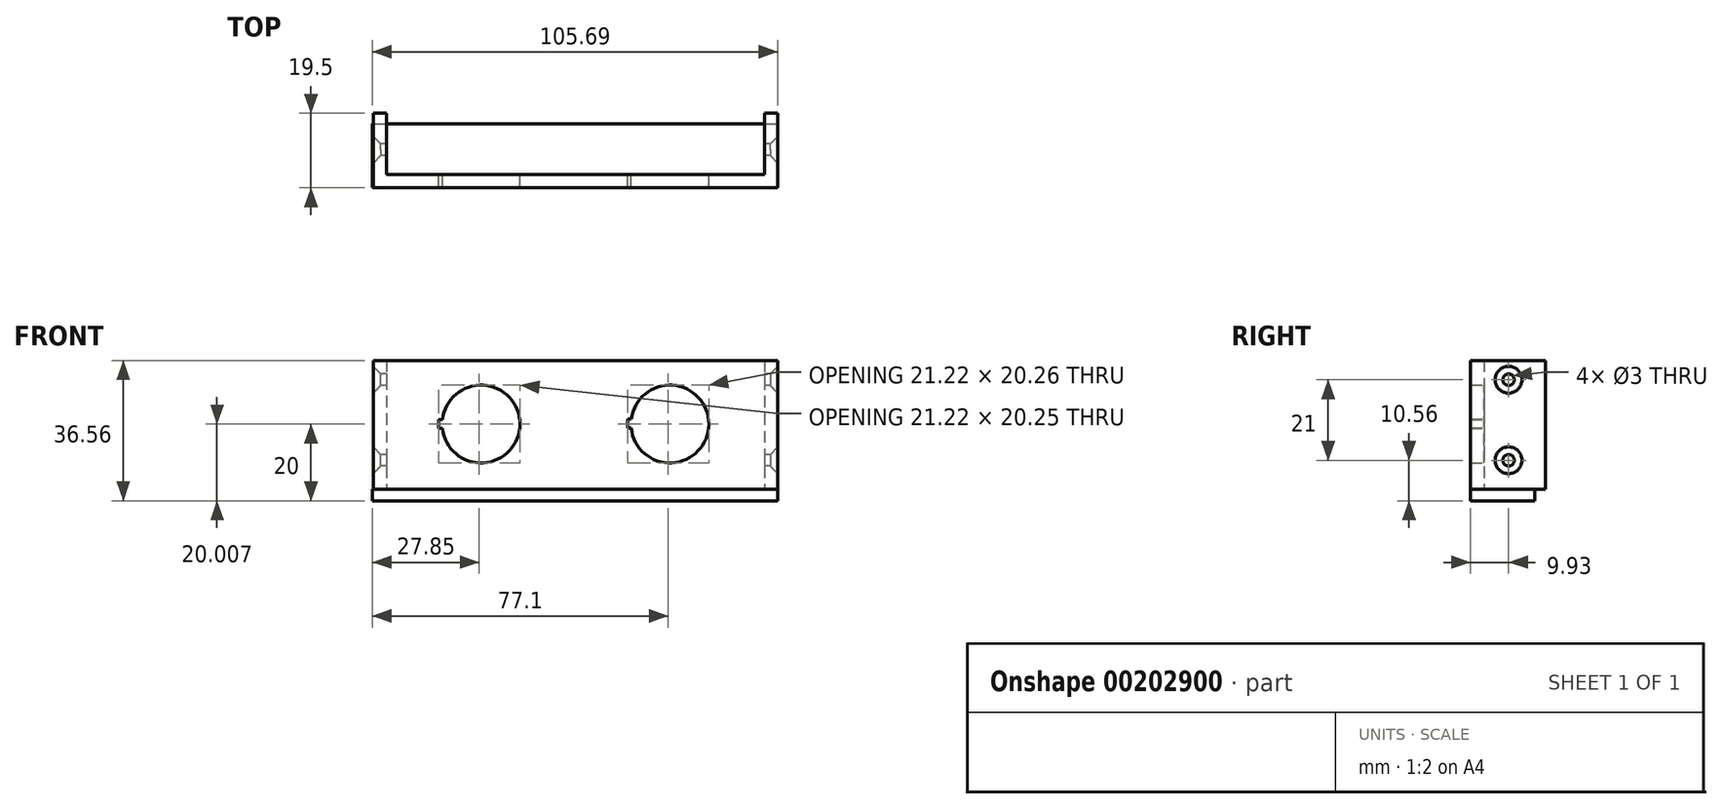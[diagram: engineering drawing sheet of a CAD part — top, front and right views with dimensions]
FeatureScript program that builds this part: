
annotation { "Feature Type Name" : "Feature", "Feature Type Description" : "" }
export const myFeature = defineFeature(function(context is Context, id is Id, definition is map)
    precondition{}
    {
        {
            var Q0;
            Q0=qCreatedBy(makeId("Front.planeOp"),FACE);
            var sketch = newSketch(context, id + "F0", { "sketchPlane" : qUnion([Q0])});
            skLineSegment(sketch, "E0.bottom", {"start": v(-49.25, 16.56) * mm, "end": v(49.25, 16.56) * mm});
            skLineSegment(sketch, "E0.top", {"start": v(-49.25, -17) * mm, "end": v(49.25, -17) * mm});
            skLineSegment(sketch, "E1", {"start": v(0, 48.82) * mm, "end": v(0, -71.11) * mm, "construction": true});
            skLineSegment(sketch, "E2", {"start": v(-61.05, 0) * mm, "end": v(79.23, 0) * mm, "construction": true});
            skLineSegment(sketch, "E3", {"start": v(-49.25, 16.56) * mm, "end": v(-49.25, -17) * mm});
            skLineSegment(sketch, "E4", {"start": v(49.25, 16.56) * mm, "end": v(49.25, -17) * mm});
            skLineSegment(sketch, "E5", {"start": v(-24.63, 20.87) * mm, "end": v(-24.62, -26.06) * mm, "construction": true});
            skLineSegment(sketch, "E6.MirrorCS", {"start": v(24.62, 20.87) * mm, "end": v(24.63, -26.06) * mm, "construction": true});
            skArc(sketch, "E7", {"start": v(-34.7, -1.15) * mm, "mid": v(-14.48, 0) * mm, "end": v(-34.7, 1.15) * mm});
            skLineSegment(sketch, "E8.bottom", {"start": v(-35.7, 1.15) * mm, "end": v(-34.7, 1.15) * mm});
            skLineSegment(sketch, "E8.top", {"start": v(-35.7, -1.15) * mm, "end": v(-34.7, -1.15) * mm});
            skLineSegment(sketch, "E8.left", {"start": v(-35.7, 1.15) * mm, "end": v(-35.7, -1.15) * mm});
            skArc(sketch, "E9", {"start": v(14.53, -1.05) * mm, "mid": v(34.77, -0.1) * mm, "end": v(14.55, 1.25) * mm});
            skLineSegment(sketch, "E10.bottom", {"start": v(13.55, 1.25) * mm, "end": v(14.55, 1.25) * mm});
            skLineSegment(sketch, "E10.top", {"start": v(13.55, -1.05) * mm, "end": v(14.53, -1.05) * mm});
            skLineSegment(sketch, "E10.left", {"start": v(13.55, 1.25) * mm, "end": v(13.55, -1.05) * mm});
            skLineSegment(sketch, "E11.MirrorCS", {"start": v(49.25, -17) * mm, "end": v(-24.62, -17) * mm});
            skPoint(sketch, "E12.orphan", {"position": v(-52.75, 16.56) * mm});
            skPoint(sketch, "E13.orphan", {"position": v(-52.75, -17) * mm});
            skPoint(sketch, "E14.orphan", {"position": v(52.75, 16.56) * mm});
            skPoint(sketch, "E15.MirrorCS.end.orphan", {"position": v(49.25, 16.56) * mm});
            skPoint(sketch, "E16.MirrorCS.end.orphan", {"position": v(52.75, -17) * mm});
            skLineSegment(sketch, "E17.bottom", {"start": v(-52.75, 16.56) * mm, "end": v(-49.25, 16.56) * mm});
            skLineSegment(sketch, "E17.top", {"start": v(-52.75, -17) * mm, "end": v(-49.25, -17) * mm});
            skLineSegment(sketch, "E17.left", {"start": v(-52.75, 16.56) * mm, "end": v(-52.75, -17) * mm});
            skLineSegment(sketch, "E18.bottom", {"start": v(49.25, 16.56) * mm, "end": v(52.75, 16.56) * mm});
            skLineSegment(sketch, "E18.top", {"start": v(49.25, -17) * mm, "end": v(52.75, -17) * mm});
            skLineSegment(sketch, "E18.right", {"start": v(52.75, 16.56) * mm, "end": v(52.75, -17) * mm});
            skSolve(sketch);
        }
        {
            var Q0;
            Q0 = qSketchRegion(id + "F0", true);
            extrude(context, id + "F1", {"entities" : qUnion([Q0]), "depth" : 3.5 * mm});
        }
        {
            var Q0;
            Q0=makeQuery(id+"F0.imprint","IMPRINT",FACE,{"disambiguationData":[TD([[makeQuery(id+"F0.imprint","IMPRINT",EDGE,{"derivedFrom":sQuery(id+"F0.wireOp",EDGE,"E3")}),-1.0]])]});
            var Q1;
            Q1=makeQuery(id+"F0.imprint","IMPRINT",FACE,{"disambiguationData":[TD([[makeQuery(id+"F0.imprint","IMPRINT",EDGE,{"derivedFrom":sQuery(id+"F0.wireOp",EDGE,"E18.bottom")}),-1.0]])]});
            extrude(context, id + "F2", {"entities" : qUnion([Q0, Q1]), "operationType" : NewBodyOperationType.ADD, "oppositeDirection" : true, "depth" : 16 * mm});
        }
        {
            var Q0;
            {var subQ0=sQuery(id+"F0.wireOp",EDGE,"E18.top");var subQ1=sQuery(id+"F0.wireOp",EDGE,"E17.top");Q0=makeQuery(id+"F2.boolean.opBoolean","MERGE",FACE,{"derivedFrom":[makeQuery(id+"F1.opExtrude","SWEPT_FACE",FACE,{"disambiguationData":[OSD([sQuery(id+"F0.wireOp",EDGE,"E0.top"),sQuery(id+"F0.wireOp",EDGE,"E11.MirrorCS"),subQ1,subQ0])]}),makeQuery(id+"F2.opExtrude","SWEPT_FACE",FACE,{"disambiguationData":[OSD([subQ1])]}),makeQuery(id+"F2.opExtrude","SWEPT_FACE",FACE,{"disambiguationData":[OSD([subQ0])]})]});}
            cPlane(context, id + "F3", {"entities" : qUnion([Q0]), "cplaneType" : CPlaneType.OFFSET, "offset" : 0 * mm, "width" : 150 * mm, "height" : 150 * mm});
        }
        {
            var Q0;
            Q0=qCreatedBy(id+"F3.planeOp",FACE);
            var sketch = newSketch(context, id + "F4", { "sketchPlane" : qUnion([Q0])});
            skLineSegment(sketch, "E19.bottom", {"start": v(-52.94, 3.5) * mm, "end": v(52.75, 3.5) * mm});
            skLineSegment(sketch, "E19.top", {"start": v(-52.94, -13.25) * mm, "end": v(52.75, -13.25) * mm});
            skLineSegment(sketch, "E19.left", {"start": v(-52.94, 3.5) * mm, "end": v(-52.94, -13.25) * mm});
            skLineSegment(sketch, "E19.right", {"start": v(52.75, 3.5) * mm, "end": v(52.75, -13.25) * mm});
            skSolve(sketch);
        }
        {
            var Q0;
            Q0 = qSketchRegion(id + "F4", true);
            extrude(context, id + "F5", {"entities" : qUnion([Q0]), "depth" : 3 * mm});
        }
        {
            var Q0;
            {var subQ0=sQuery(id+"F0.wireOp",EDGE,"E17.left");Q0=makeQuery(id+"F2.boolean.opBoolean","MERGE",FACE,{"derivedFrom":[makeQuery(id+"F1.opExtrude","SWEPT_FACE",FACE,{"disambiguationData":[OSD([subQ0])]}),makeQuery(id+"F2.opExtrude","SWEPT_FACE",FACE,{"disambiguationData":[OSD([subQ0])]})]});}
            cPlane(context, id + "F6", {"entities" : qUnion([Q0]), "cplaneType" : CPlaneType.OFFSET, "offset" : 25 * mm, "width" : 150 * mm, "height" : 150 * mm});
        }
        {
            var Q0;
            Q0=qCreatedBy(id+"F6.planeOp",FACE);
            var sketch = newSketch(context, id + "F7", { "sketchPlane" : qUnion([Q0])});
            skLineSegment(sketch, "E20", {"start": v(0, 26.8) * mm, "end": v(0, -25.8) * mm, "construction": true});
            skLineSegment(sketch, "E21", {"start": v(-6.43, 26.8) * mm, "end": v(-6.43, -25.8) * mm, "construction": true});
            skLineSegment(sketch, "E22", {"start": v(-11.6, 11.56) * mm, "end": v(8.73, 11.56) * mm, "construction": true});
            skLineSegment(sketch, "E23", {"start": v(-9.6, -9.44) * mm, "end": v(10.6, -9.44) * mm, "construction": true});
            skCircle(sketch, "E24", {"center": v(-6.43, 11.56) * mm, "radius": 1.5 * mm});
            skCircle(sketch, "E25", {"center": v(-6.43, -9.44) * mm, "radius": 1.5 * mm});
            skSolve(sketch);
        }
        {
            var Q0;
            Q0 = qSketchRegion(id + "F7", true);
            extrude(context, id + "F8", {"entities" : qUnion([Q0]), "operationType" : NewBodyOperationType.REMOVE, "oppositeDirection" : true, "depth" : 150 * mm});
        }
        {
            var Q0;
            {var subQ0=sQuery(id+"F0.wireOp",EDGE,"E18.right");Q0=makeQuery(id+"F8.boolean.opBoolean","INTERSECT",EDGE,{"derivedFrom":[makeQuery(id+"F2.boolean.opBoolean","MERGE",FACE,{"derivedFrom":[makeQuery(id+"F1.opExtrude","SWEPT_FACE",FACE,{"disambiguationData":[OSD([subQ0])]}),makeQuery(id+"F2.opExtrude","SWEPT_FACE",FACE,{"disambiguationData":[OSD([subQ0])]})]}),makeQuery(id+"F8.opExtrude","SWEPT_FACE",FACE,{"disambiguationData":[OSD([sQuery(id+"F7.wireOp",EDGE,"E24")])]})]});}
            var Q1;
            {var subQ0=sQuery(id+"F0.wireOp",EDGE,"E18.right");Q1=makeQuery(id+"F8.boolean.opBoolean","INTERSECT",EDGE,{"derivedFrom":[makeQuery(id+"F2.boolean.opBoolean","MERGE",FACE,{"derivedFrom":[makeQuery(id+"F1.opExtrude","SWEPT_FACE",FACE,{"disambiguationData":[OSD([subQ0])]}),makeQuery(id+"F2.opExtrude","SWEPT_FACE",FACE,{"disambiguationData":[OSD([subQ0])]})]}),makeQuery(id+"F8.opExtrude","SWEPT_FACE",FACE,{"disambiguationData":[OSD([sQuery(id+"F7.wireOp",EDGE,"E25")])]})]});}
            var Q2;
            {var subQ0=sQuery(id+"F0.wireOp",EDGE,"E17.left");Q2=makeQuery(id+"F8.boolean.opBoolean","INTERSECT",EDGE,{"derivedFrom":[makeQuery(id+"F2.boolean.opBoolean","MERGE",FACE,{"derivedFrom":[makeQuery(id+"F1.opExtrude","SWEPT_FACE",FACE,{"disambiguationData":[OSD([subQ0])]}),makeQuery(id+"F2.opExtrude","SWEPT_FACE",FACE,{"disambiguationData":[OSD([subQ0])]})]}),makeQuery(id+"F8.opExtrude","SWEPT_FACE",FACE,{"disambiguationData":[OSD([sQuery(id+"F7.wireOp",EDGE,"E24")])]})]});}
            var Q3;
            {var subQ0=sQuery(id+"F0.wireOp",EDGE,"E17.left");Q3=makeQuery(id+"F8.boolean.opBoolean","INTERSECT",EDGE,{"derivedFrom":[makeQuery(id+"F2.boolean.opBoolean","MERGE",FACE,{"derivedFrom":[makeQuery(id+"F1.opExtrude","SWEPT_FACE",FACE,{"disambiguationData":[OSD([subQ0])]}),makeQuery(id+"F2.opExtrude","SWEPT_FACE",FACE,{"disambiguationData":[OSD([subQ0])]})]}),makeQuery(id+"F8.opExtrude","SWEPT_FACE",FACE,{"disambiguationData":[OSD([sQuery(id+"F7.wireOp",EDGE,"E25")])]})]});}
            chamfer(context, id + "F9", {"entities" : qUnion([Q0, Q1, Q2, Q3]), "width" : 2 * mm, "tangentPropagation" : true});
        }
    });
